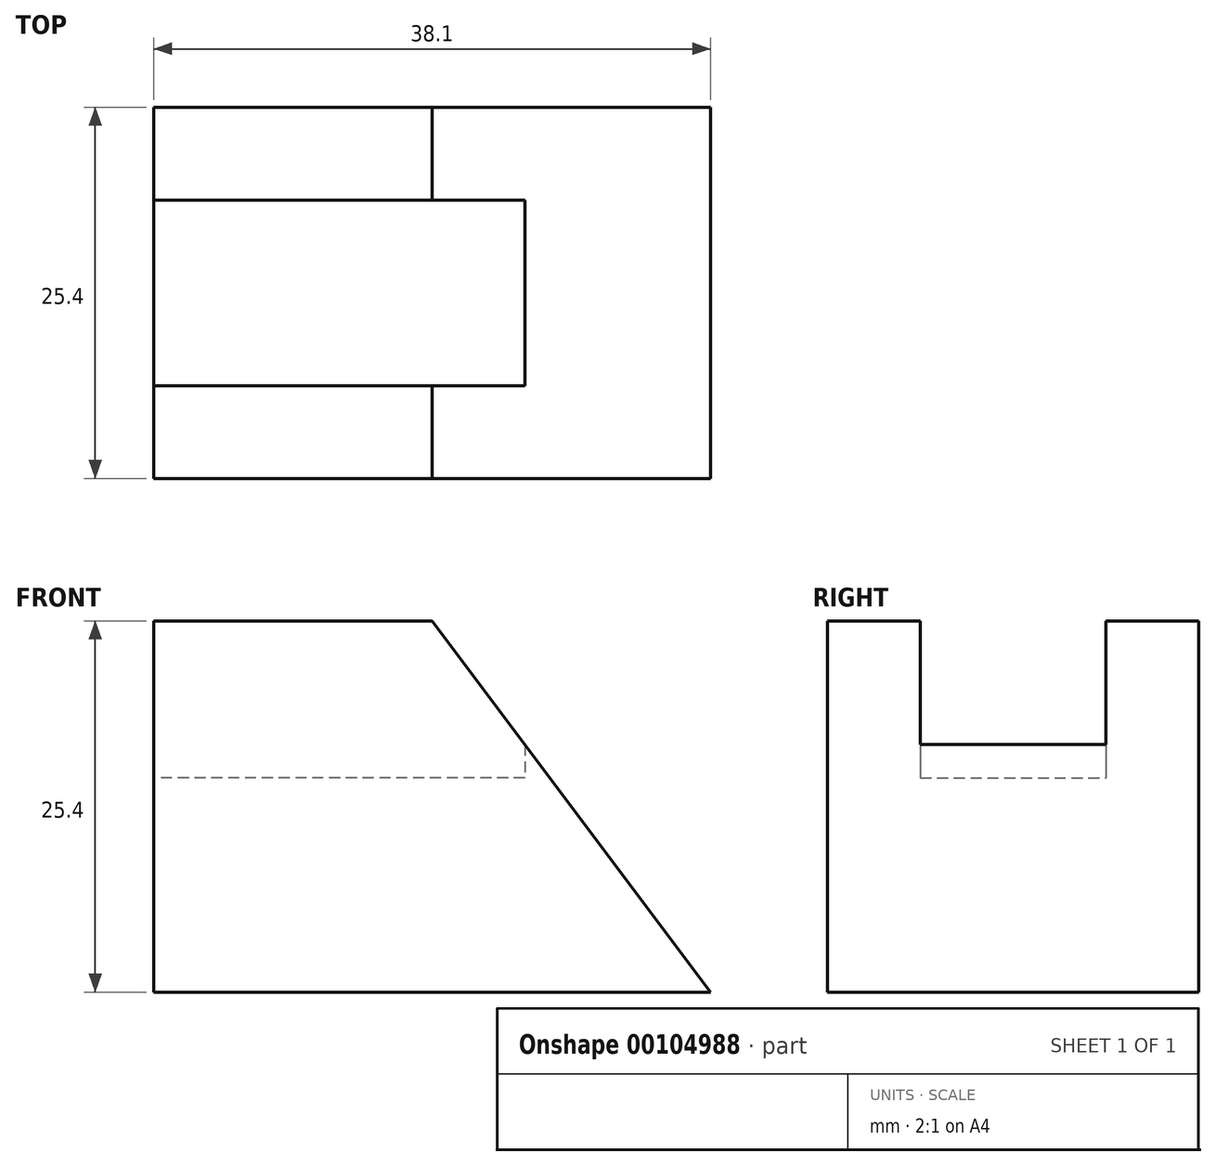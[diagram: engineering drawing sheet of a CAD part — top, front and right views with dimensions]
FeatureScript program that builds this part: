
annotation { "Feature Type Name" : "Feature", "Feature Type Description" : "" }
export const myFeature = defineFeature(function(context is Context, id is Id, definition is map)
    precondition{}
    {
        {
            var Q0;
            Q0=qCreatedBy(makeId("Front.planeOp"),FACE);
            var sketch = newSketch(context, id + "F0", { "sketchPlane" : qUnion([Q0])});
            skLineSegment(sketch, "E0.bottom", {"start": v(0, 0) * mm, "end": v(38.1, 0) * mm});
            skLineSegment(sketch, "E0.top", {"start": v(0, 25.4) * mm, "end": v(19.05, 25.4) * mm});
            skLineSegment(sketch, "E0.left", {"start": v(0, 0) * mm, "end": v(0, 25.4) * mm});
            skLineSegment(sketch, "E1", {"start": v(19.05, 25.4) * mm, "end": v(38.1, 0) * mm});
            skSolve(sketch);
        }
        {
            var Q0;
            Q0=qCreatedBy(makeId("Right.planeOp"),FACE);
            var sketch = newSketch(context, id + "F1", { "sketchPlane" : qUnion([Q0])});
            skLineSegment(sketch, "E2.top", {"start": v(6.35, 14.67) * mm, "end": v(19.05, 14.67) * mm});
            skLineSegment(sketch, "E2.left", {"start": v(6.35, 25.4) * mm, "end": v(6.35, 14.67) * mm});
            skLineSegment(sketch, "E2.right", {"start": v(19.05, 25.4) * mm, "end": v(19.05, 14.67) * mm});
            skLineSegment(sketch, "E3", {"start": v(6.35, 25.4) * mm, "end": v(19.05, 25.4) * mm});
            skPoint(sketch, "E4.bottom.end.orphan", {"position": v(25.4, 0) * mm});
            skPoint(sketch, "E4.bottom.start.orphan", {"position": v(0, 0) * mm});
            skPoint(sketch, "E5.end.orphan", {"position": v(25.4, 25.4) * mm});
            skPoint(sketch, "E6.start.orphan", {"position": v(0, 25.4) * mm});
            skSolve(sketch);
        }
        {
            var Q0;
            Q0 = qSketchRegion(id + "F0", true);
            extrude(context, id + "F2", {"entities" : qUnion([Q0]), "oppositeDirection" : true, "depth" : 25.4 * mm});
        }
        {
            var Q0;
            Q0 = qSketchRegion(id + "F1", true);
            extrude(context, id + "F3", {"entities" : qUnion([Q0]), "operationType" : NewBodyOperationType.REMOVE, "depth" : 25.4 * mm});
        }
    });
